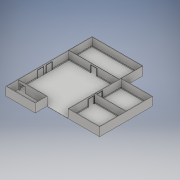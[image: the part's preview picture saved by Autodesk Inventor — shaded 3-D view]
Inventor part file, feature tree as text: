
AUTODESK INVENTOR PART (.ipt)
format: ipt  version: 2017 (Build 210142000, 142)  size: 660,480 bytes
history: native  units: in
note: dims shown in document units (in); Inventor stores cm internally (conversion verified against a paired STEP export)
features: sketch x47, extrude x46, fillet x2, other x1
ambient origin geometry x8: Origin, YZ Plane, XZ Plane, XY Plane, X Axis, Y Axis, Z Axis, Center Point
bodies: Solid1 (feature_tree)
feature tree (96):
  extrude  "Door Frame CR"  Depth=7.5in
  extrude  "Door Frame left Extruded"  Depth=11.0in
  extrude  "Door Frame right Extruded"  Depth=0.35in TaperAngle=0.0deg
  extrude  "Floor"  Depth=27.0in TaperAngle=0.0deg
  extrude  "Walls"  Depth=30.0in TaperAngle=0.0deg
  extrude  "Door Fram ex"  Depth=10.8125in TaperAngle=0.0deg
  fillet  "Dorr Fillet"  Radius=0.3in
  fillet  "Door Fillet"  Radius=0.3in
  extrude  "Door floor"  Depth=0.3125in TaperAngle=0.0deg
  extrude  "wall board middle"  Depth=0.02in
  extrude  "Wall board left"  Depth=0.35in
  extrude  "Wall board right"  Depth=1.455in
  extrude  "Wall board door"  Depth=1.4574in
  extrude  "Door mid"  Depth=0.1in TaperAngle=0.0deg
  extrude  "Main wall left"  Depth=0.1in TaperAngle=0.0deg
  extrude  "Main wall right"  Depth=65.5in
  extrude  "prob the floor"  Depth=65.5in
  extrude  "wall board front main 1"  TaperAngle=0.0deg  [1 undecoded]
  extrude  "wall board front main 2"  TaperAngle=0.0deg  [1 undecoded]
  extrude  "wall board front left"  Depth=0.1in TaperAngle=0.0deg
  extrude  "wall board front right"  Depth=0.1in TaperAngle=0.0deg
  extrude  "Right doors"  Depth=7.5in
  sketch  "Sketch33"  dims[d67=0.1in d68=0.0in d69=7.5in]
  extrude  "Right doors head"  Depth=11.0in
  sketch  "Sketch35"  dims[d72=11.0in d73=3.0in d74=0.05in d75=0.0in d76=0.0in]
  extrude  "Right doors frame mid"  Depth=0.05in TaperAngle=0.0deg
  extrude  "right doors frame into"  Depth=1.72in
  extrude  "Room 2 & 3 wall "  Depth=0.3049in
  extrude  "Room 3 wall right"  Depth=0.3in TaperAngle=0.0deg
  extrude  "Room 3 wall mid"  Depth=40.0in TaperAngle=0.0deg
  extrude  "Room 3 Floor"  Depth=0.6in
  extrude  "Room 2 mid wall"  Depth=40.0in TaperAngle=0.0deg
  extrude  "Room 2 wall left"  Depth=10.8in
  extrude  "Room 2 floor"  Depth=40.0in TaperAngle=0.0deg
  extrude  "Room 2 wall board left"  Depth=10.8in
  extrude  "Room 3 wall board left"  Depth=0.6in
  extrude  "Room 2 & 3 wall board mid"  Depth=39.9in TaperAngle=0.0deg
  extrude  "Room 3 wall board right"  Depth=1.255in
  extrude  "Room 2 wall board right"  Depth=1.255in
  extrude  "Room 3 wall board door"  Depth=1.255in
  extrude  "Room 2 wall board door"  Depth=1.255in
  extrude  "Fake Door Frame"  Depth=1.255in
  extrude  "My mistake ;-;"  Depth=1.255in
  extrude  "Closet main wall"  Depth=0.1in TaperAngle=0.0deg
  extrude  "Closet left and right wall"  Depth=0.15in TaperAngle=0.0deg
  extrude  "Closet back wall"  Depth=37.0in TaperAngle=0.0deg
  extrude  "Closet Floor"  Depth=0.6in
  extrude  "Closet Outter wall board"  Depth=0.6in
  extrude  "Closet Door Frame"  Depth=15.0in TaperAngle=0.0deg
  extrude  "Extrusion47"  Depth=0.315in TaperAngle=0.0deg
  sketch  "Sketch1"  dims[d0=9.0in d1=7.5in]
  sketch  "Sketch2"  dims[d2=2.0in d3=11.0in]
  sketch  "Sketch4"  dims[d4=11.5in d5=0.35in d6=0.0in]
  sketch  "Sketch5"  dims[d7=27.0in d8=0.0in d9=27.0in d10=0.0in]
  sketch  "Sketch7"  dims[d11=0.2in d12=30.0in d13=0.0in]
  other  "Door Frame"
  sketch  "Sketch9"  dims[d21=0.5in d22=10.8125in d23=0.0in d27=0.3in d28=0.3in]
  sketch  "Sketch13"  dims[d29=0.3in d30=0.3125in d31=0.0in]
  sketch  "Sketch14"  dims[d32=0.02in d33=0.02in]
  sketch  "Sketch16"  dims[d34=0.35in d35=0.0in d36=1.3in]
  sketch  "Sketch20"  dims[d37=0.1in d38=0.0in d39=1.455in]
  sketch  "Sketch22"  dims[d40=0.1in d41=0.0in d42=1.4574in]
  sketch  "Sketch23"  dims[d43=1.457in d44=0.1in d45=0.0in]
  sketch  "Sketch24"  dims[d47=1.457in d49=0.1in d50=0.0in]
  sketch  "Sketch26"  dims[d51=0.35in d52=0.0in d53=65.5in]
  sketch  "Sketch27"  dims[d54=0.0in d55=65.5in]
  sketch  "Sketch28"  dims[d56=65.5in d57=0.0in]
  sketch  "Sketch30"  dims[d58=65.5in d59=0.0in]
  sketch  "Sketch31"  dims[d60=1.4574in d61=0.1in d62=0.0in]
  sketch  "Sketch32"  dims[d63=0.1in d64=0.0in d65=0.1in d66=0.0in]
  sketch  "Sketch34"  dims[d70=7.5in d71=11.0in]
  sketch  "Sketch36"  dims[d77=1.72in d78=1.72in]
  sketch  "Sketch38"  dims[d79=20.375in d80=0.0in d81=0.3049in]
  sketch  "Sketch41"  dims[d82=0.3049in d87=0.3in d88=0.0in]
  sketch  "Sketch44"  dims[d90=0.3in d91=0.0in d94=40.0in d95=0.0in]
  sketch  "Sketch45"  dims[d96=10.8in d97=0.6in]
  sketch  "Sketch47"  dims[d98=10.8in d99=40.0in d100=0.0in]
  sketch  "Sketch48"  dims[d101=0.6in d102=10.8in]
  sketch  "Sketch49"  dims[d103=33.5in d104=0.0in d105=40.0in d106=0.0in]
  sketch  "Sketch50"  dims[d107=0.6in d108=10.8in]
  sketch  "Sketch54"  dims[d109=33.5in d110=0.0in d111=0.6in]
  sketch  "Sketch55"  dims[d112=10.8in d113=39.9in d114=0.0in]
  sketch  "Sketch56"  dims[d115=40.0in d116=0.0in d117=1.255in]
  sketch  "Sketch57"  dims[d118=0.1in d119=0.0in d120=1.255in]
  sketch  "Sketch58"  dims[d121=0.1in d122=0.0in d123=1.255in]
  sketch  "Sketch59"  dims[d124=0.1in d125=0.0in d126=1.255in]
  sketch  "Sketch60"  dims[d127=0.1in d128=0.0in d129=1.255in]
  sketch  "Sketch62"  dims[d130=0.1in d131=0.0in d132=1.255in]
  sketch  "Sketch64"  dims[d133=0.1in d134=0.0in d135=0.1in d136=0.0in]
  sketch  "Sketch67"  dims[d137=0.315in d138=0.0in d139=0.15in d140=0.0in]
  sketch  "Sketch68"  dims[d141=0.6in d142=37.0in d143=0.0in]
  sketch  "Sketch69"  dims[d144=0.6in d145=0.6in]
  sketch  "Sketch70"  dims[d146=15.0in d147=0.0in d148=0.6in]
  sketch  "Sketch73"  dims[d149=36.4375in d150=0.0in d151=15.0in d152=0.0in]
  sketch  "Sketch74"  dims[d153=0.15in d154=0.0in d160=0.315in d161=0.0in]
  sketch  "Sketch76"  dims[d162=3.0in d163=0.0in]
note: 2 required parameter values undecoded (feature->parameter linkage not recoverable at this tier; creation-order binding heuristic only, values carry confidence <= 0.55)
